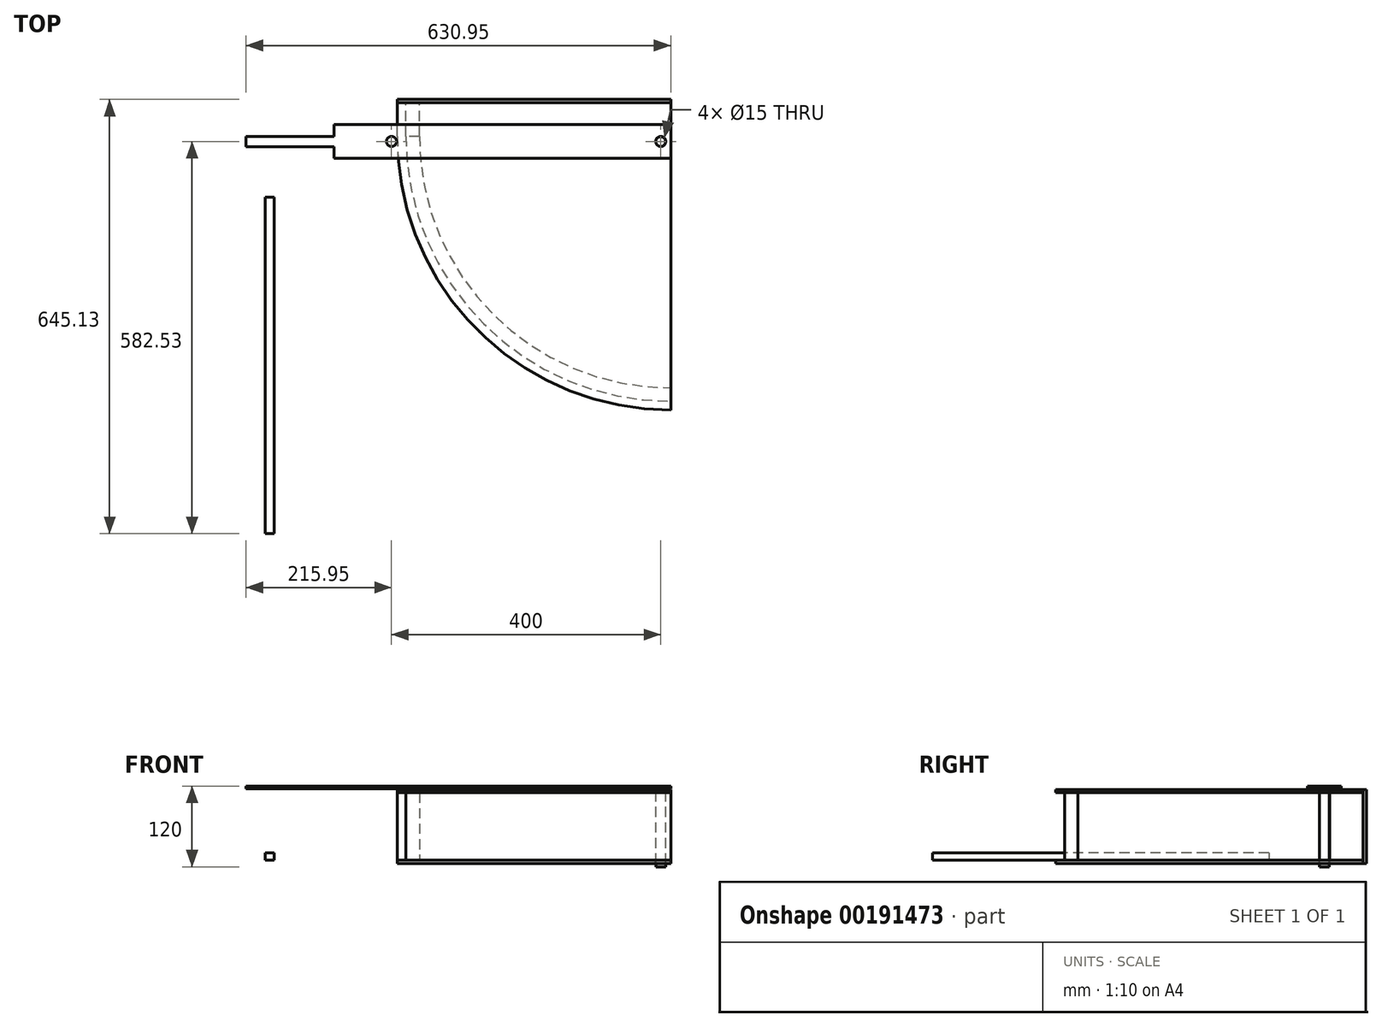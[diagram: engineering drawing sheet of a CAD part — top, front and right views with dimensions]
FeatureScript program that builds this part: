
annotation { "Feature Type Name" : "Feature", "Feature Type Description" : "" }
export const myFeature = defineFeature(function(context is Context, id is Id, definition is map)
    precondition{}
    {
        {
            var Q0;
            Q0=qCreatedBy(makeId("Top.planeOp"),FACE);
            var sketch = newSketch(context, id + "F0", { "sketchPlane" : qUnion([Q0])});
            skLineSegment(sketch, "E0", {"start": v(0, 0) * mm, "end": v(-393.5, 0) * mm});
            skArc(sketch, "E1", {"start": v(-393.5, 0) * mm, "mid": v(-278.25, -278.25) * mm, "end": v(0, -393.5) * mm});
            skLineSegment(sketch, "E2", {"start": v(0, 0) * mm, "end": v(0, -393.5) * mm});
            skArc(sketch, "E3.0", {"start": v(-373.5, 0) * mm, "mid": v(-264.1, -264.1) * mm, "end": v(0, -373.5) * mm});
            skLineSegment(sketch, "E4.top", {"start": v(-393.5, 50) * mm, "end": v(-373.5, 50) * mm});
            skLineSegment(sketch, "E4.left", {"start": v(-393.5, 0) * mm, "end": v(-393.5, 50) * mm});
            skLineSegment(sketch, "E4.right", {"start": v(-373.5, 0) * mm, "end": v(-373.5, 50) * mm});
            skSolve(sketch);
        }
        {
            var Q0;
            {var subQ0=sQuery(id+"F0.wireOp",EDGE,"E1");Q0=makeQuery(id+"F0.imprint","IMPRINT",FACE,{"disambiguationData":[TD([[makeQuery(id+"F0.imprint","IMPRINT",EDGE,{"derivedFrom":subQ0}),1.0]])]});}
            var Q1;
            Q1=makeQuery(id+"F0.imprint","IMPRINT",FACE,{"disambiguationData":[TD([[makeQuery(id+"F0.imprint","IMPRINT",EDGE,{"derivedFrom":sQuery(id+"F0.wireOp",EDGE,"E4.bottom")}),1.0]])]});
            extrude(context, id + "F1", {"entities" : qUnion([Q0, Q1]), "depth" : 100 * mm});
        }
        {
            var Q0;
            Q0=makeQuery(id+"F1.opExtrude","CAP_FACE",FACE,{"disambiguationData":[OSD([sQuery(id+"F0.wireOp",EDGE,"E0"),sQuery(id+"F0.wireOp",EDGE,"E1"),sQuery(id+"F0.wireOp",EDGE,"E2"),sQuery(id+"F0.wireOp",EDGE,"E3.0")])],"isStart":true});
            cPlane(context, id + "F2", {"entities" : qUnion([Q0]), "cplaneType" : CPlaneType.OFFSET, "offset" : 0 * mm, "width" : 150 * mm, "height" : 150 * mm});
        }
        {
            var Q0;
            Q0=qCreatedBy(id+"F2.planeOp",FACE);
            var sketch = newSketch(context, id + "F3", { "sketchPlane" : qUnion([Q0])});
            skLineSegment(sketch, "E5", {"start": v(0, 0) * mm, "end": v(0, 406.5) * mm});
            skLineSegment(sketch, "E6", {"start": v(0, 0) * mm, "end": v(-406.5, 0) * mm});
            skArc(sketch, "E7", {"start": v(0, 393.5) * mm, "mid": v(-278.25, 278.25) * mm, "end": v(-393.5, 0) * mm});
            skArc(sketch, "E8.0", {"start": v(0, 406.5) * mm, "mid": v(-287.44, 287.44) * mm, "end": v(-406.5, 0) * mm});
            skLineSegment(sketch, "E9.bottom", {"start": v(-406.5, 0) * mm, "end": v(0, 0) * mm});
            skLineSegment(sketch, "E9.top", {"start": v(-406.5, -50) * mm, "end": v(0, -50) * mm});
            skLineSegment(sketch, "E9.right", {"start": v(0, 0) * mm, "end": v(0, -50) * mm});
            skLineSegment(sketch, "E10", {"start": v(-406.5, 0) * mm, "end": v(-406.5, -50) * mm});
            skSolve(sketch);
        }
        {
            var Q0;
            Q0=qSketchRegion(id+"F3",true);
            extrude(context, id + "F4", {"entities" : qUnion([Q0]), "depth" : 5 * mm});
        }
        {
            var Q0;
            Q0=makeQuery(id+"F1.opExtrude","CAP_FACE",FACE,{"disambiguationData":[OSD([sQuery(id+"F0.wireOp",EDGE,"E0"),sQuery(id+"F0.wireOp",EDGE,"E1"),sQuery(id+"F0.wireOp",EDGE,"E2"),sQuery(id+"F0.wireOp",EDGE,"E3.0")])],"isStart":false});
            cPlane(context, id + "F5", {"entities" : qUnion([Q0]), "cplaneType" : CPlaneType.OFFSET, "offset" : 0 * mm, "width" : 150 * mm, "height" : 150 * mm});
        }
        {
            var Q0;
            Q0=qCreatedBy(id+"F5.planeOp",FACE);
            var sketch = newSketch(context, id + "F6", { "sketchPlane" : qUnion([Q0])});
            skLineSegment(sketch, "E11", {"start": v(0, 0) * mm, "end": v(0, -393.5) * mm});
            skLineSegment(sketch, "E12", {"start": v(0, 0) * mm, "end": v(-393.5, 0) * mm});
            skArc(sketch, "E13.0", {"start": v(-393.5, 0) * mm, "mid": v(-278.25, -278.25) * mm, "end": v(0, -393.5) * mm});
            skLineSegment(sketch, "E14.bottom", {"start": v(-393.5, 0) * mm, "end": v(0, 0) * mm});
            skLineSegment(sketch, "E14.top", {"start": v(-393.5, 50) * mm, "end": v(0, 50) * mm});
            skLineSegment(sketch, "E14.left", {"start": v(-393.5, 0) * mm, "end": v(-393.5, 50) * mm});
            skLineSegment(sketch, "E14.right", {"start": v(0, 0) * mm, "end": v(0, 50) * mm});
            skLineSegment(sketch, "E15", {"start": v(0, -393.5) * mm, "end": v(0, -406.5) * mm});
            skArc(sketch, "E16", {"start": v(-406.5, 0) * mm, "mid": v(-287.44, -287.44) * mm, "end": v(0, -406.5) * mm});
            skLineSegment(sketch, "E17", {"start": v(-393.5, 0) * mm, "end": v(-406.5, 0) * mm});
            skLineSegment(sketch, "E18", {"start": v(-406.5, 0) * mm, "end": v(-406.5, 50) * mm});
            skLineSegment(sketch, "E19", {"start": v(-406.5, 50) * mm, "end": v(-393.5, 50) * mm});
            skSolve(sketch);
        }
        {
            var Q0;
            Q0=qSketchRegion(id+"F6",true);
            extrude(context, id + "F7", {"entities" : qUnion([Q0]), "depth" : 5 * mm});
        }
        {
            var Q0;
            Q0=makeQuery(id+"F4.opExtrude","SWEPT_FACE",FACE,{"disambiguationData":[OSD([sQuery(id+"F3.wireOp",EDGE,"E9.top")])]});
            cPlane(context, id + "F8", {"entities" : qUnion([Q0]), "cplaneType" : CPlaneType.OFFSET, "offset" : 0 * mm, "width" : 150 * mm, "height" : 150 * mm});
        }
        {
            var Q0;
            Q0=qCreatedBy(id+"F8.planeOp",FACE);
            var sketch = newSketch(context, id + "F9", { "sketchPlane" : qUnion([Q0])});
            skLineSegment(sketch, "E20", {"start": v(0, -5) * mm, "end": v(0, 105) * mm});
            skLineSegment(sketch, "E21", {"start": v(0, -5) * mm, "end": v(406.5, -5) * mm});
            skLineSegment(sketch, "E22", {"start": v(406.5, -5) * mm, "end": v(406.5, 105) * mm});
            skLineSegment(sketch, "E23", {"start": v(406.5, 105) * mm, "end": v(0, 105) * mm});
            skSolve(sketch);
        }
        {
            var Q0;
            Q0=qSketchRegion(id+"F9",true);
            extrude(context, id + "F10", {"entities" : qUnion([Q0]), "depth" : 5.1 * mm});
        }
        {
            var Q0;
            Q0=makeQuery(id+"F7.opExtrude","CAP_FACE",FACE,{"disambiguationData":[OSD([sQuery(id+"F6.wireOp",EDGE,"E11"),sQuery(id+"F6.wireOp",EDGE,"E13.0"),sQuery(id+"F6.wireOp",EDGE,"E14.top"),sQuery(id+"F6.wireOp",EDGE,"E14.left"),sQuery(id+"F6.wireOp",EDGE,"E14.right")])],"isStart":false});
            var sketch = newSketch(context, id + "F11", { "sketchPlane" : qUnion([Q0])});
            skCircle(sketch, "E24", {"center": v(-15, -7.5) * mm, "radius": 7.5 * mm});
            skSolve(sketch);
        }
        {
            var Q0;
            Q0=qSketchRegion(id+"F11",true);
            extrude(context, id + "F12", {"entities" : qUnion([Q0]), "operationType" : NewBodyOperationType.REMOVE, "endBound" : BoundingType.THROUGH_ALL, "oppositeDirection" : true, "depth" : 42 * mm});
        }
        {
            var Q0;
            Q0=makeQuery(id+"F7.opExtrude","CAP_FACE",FACE,{"disambiguationData":[OSD([sQuery(id+"F6.wireOp",EDGE,"E11"),sQuery(id+"F6.wireOp",EDGE,"E13.0"),sQuery(id+"F6.wireOp",EDGE,"E14.top"),sQuery(id+"F6.wireOp",EDGE,"E14.left"),sQuery(id+"F6.wireOp",EDGE,"E14.right")])],"isStart":false});
            cPlane(context, id + "F13", {"entities" : qUnion([Q0]), "cplaneType" : CPlaneType.OFFSET, "offset" : 5 * mm, "width" : 150 * mm, "height" : 150 * mm});
        }
        {
            var Q0;
            Q0=qCreatedBy(id+"F13.planeOp",FACE);
            var sketch = newSketch(context, id + "F14", { "sketchPlane" : qUnion([Q0])});
            skCircle(sketch, "E25", {"center": v(-15, -7.5) * mm, "radius": 7.25 * mm});
            skSolve(sketch);
        }
        {
            var Q0;
            Q0=qSketchRegion(id+"F14",true);
            extrude(context, id + "F15", {"entities" : qUnion([Q0]), "oppositeDirection" : true, "depth" : 120 * mm});
        }
        {
            var Q0;
            Q0=makeQuery(id+"F15.opExtrude","CAP_FACE",FACE,{"disambiguationData":[OSD([sQuery(id+"F14.wireOp",EDGE,"E25")])],"isStart":true});
            cPlane(context, id + "F16", {"entities" : qUnion([Q0]), "cplaneType" : CPlaneType.OFFSET, "offset" : 0 * mm, "width" : 150 * mm, "height" : 150 * mm});
        }
        {
            var Q0;
            Q0=qCreatedBy(id+"F16.planeOp",FACE);
            var sketch = newSketch(context, id + "F17", { "sketchPlane" : qUnion([Q0])});
            skLineSegment(sketch, "E26.bottom", {"start": v(0, -32.5) * mm, "end": v(-500, -32.5) * mm});
            skLineSegment(sketch, "E26.top", {"start": v(0, 17.5) * mm, "end": v(-500, 17.5) * mm});
            skLineSegment(sketch, "E26.left", {"start": v(0, -32.5) * mm, "end": v(0, 17.5) * mm});
            skLineSegment(sketch, "E26.right", {"start": v(-500, -32.5) * mm, "end": v(-500, 17.5) * mm});
            skCircle(sketch, "E27", {"center": v(-15, -7.5) * mm, "radius": 7.5 * mm});
            skCircle(sketch, "E28", {"center": v(-415, -7.5) * mm, "radius": 7.5 * mm});
            skLineSegment(sketch, "E29.bottom", {"start": v(-500, 0) * mm, "end": v(-630.95, 0) * mm});
            skLineSegment(sketch, "E29.top", {"start": v(-500, -15) * mm, "end": v(-630.95, -15) * mm});
            skLineSegment(sketch, "E29.left", {"start": v(-500, 0) * mm, "end": v(-500, -15) * mm});
            skLineSegment(sketch, "E29.right", {"start": v(-630.95, 0) * mm, "end": v(-630.95, -15) * mm});
            skSolve(sketch);
        }
        {
            var Q0;
            Q0=qSketchRegion(id+"F17",true);
            extrude(context, id + "F18", {"entities" : qUnion([Q0]), "operationType" : NewBodyOperationType.ADD, "oppositeDirection" : true, "depth" : 4 * mm});
        }
        {
            var Q0;
            Q0=makeQuery(id+"F0.imprint","IMPRINT",FACE,{"disambiguationData":[TD([[makeQuery(id+"F0.imprint","IMPRINT",EDGE,{"derivedFrom":sQuery(id+"F0.wireOp",EDGE,"E4.top")}),-1.0]])]});
            extrude(context, id + "F19", {"entities" : qUnion([Q0]), "depth" : 100 * mm});
        }
        {
            var Q0;
            Q0=makeQuery(id+"F18.opExtrude","CAP_FACE",FACE,{"disambiguationData":[OSD([sQuery(id+"F17.wireOp",EDGE,"E26.bottom"),sQuery(id+"F17.wireOp",EDGE,"E26.top"),sQuery(id+"F17.wireOp",EDGE,"E26.left"),sQuery(id+"F17.wireOp",EDGE,"E26.right"),sQuery(id+"F17.wireOp",EDGE,"E27"),sQuery(id+"F17.wireOp",EDGE,"E28")])],"isStart":false});
            var sketch = newSketch(context, id + "F20", { "sketchPlane" : qUnion([Q0])});
            skCircle(sketch, "E30", {"center": v(-415, 7.5) * mm, "radius": 7.5 * mm});
            skCircle(sketch, "E31", {"center": v(-415, 7.5) * mm, "radius": 11 * mm});
            skSolve(sketch);
        }
        {
            var Q0;
            Q0=qCreatedBy(makeId("Top.planeOp"),FACE);
            var sketch = newSketch(context, id + "F21", { "sketchPlane" : qUnion([Q0])});
            skLineSegment(sketch, "E32.bottom", {"start": v(-602.48, -90.03) * mm, "end": v(-589.48, -90.03) * mm});
            skLineSegment(sketch, "E32.top", {"start": v(-602.48, -590.03) * mm, "end": v(-589.48, -590.03) * mm});
            skLineSegment(sketch, "E32.left", {"start": v(-602.48, -90.03) * mm, "end": v(-602.48, -590.03) * mm});
            skLineSegment(sketch, "E32.right", {"start": v(-589.48, -90.03) * mm, "end": v(-589.48, -590.03) * mm});
            skSolve(sketch);
        }
        {
            var Q0;
            Q0=qSketchRegion(id+"F21",true);
            extrude(context, id + "F22", {"entities" : qUnion([Q0]), "depth" : 11 * mm});
        }
        {
            var Q0;
            Q0=sQuery(id+"F20.wireOp",EDGE,"E31");
            var Q1;
            Q1=sQuery(id+"F20.wireOp",EDGE,"E30");
            extrude(context, id + "F23", {"bodyType" : ToolBodyType.SURFACE, "surfaceEntities" : qUnion([Q0, Q1]), "depth" : 111.5 * mm});
        }
    });
